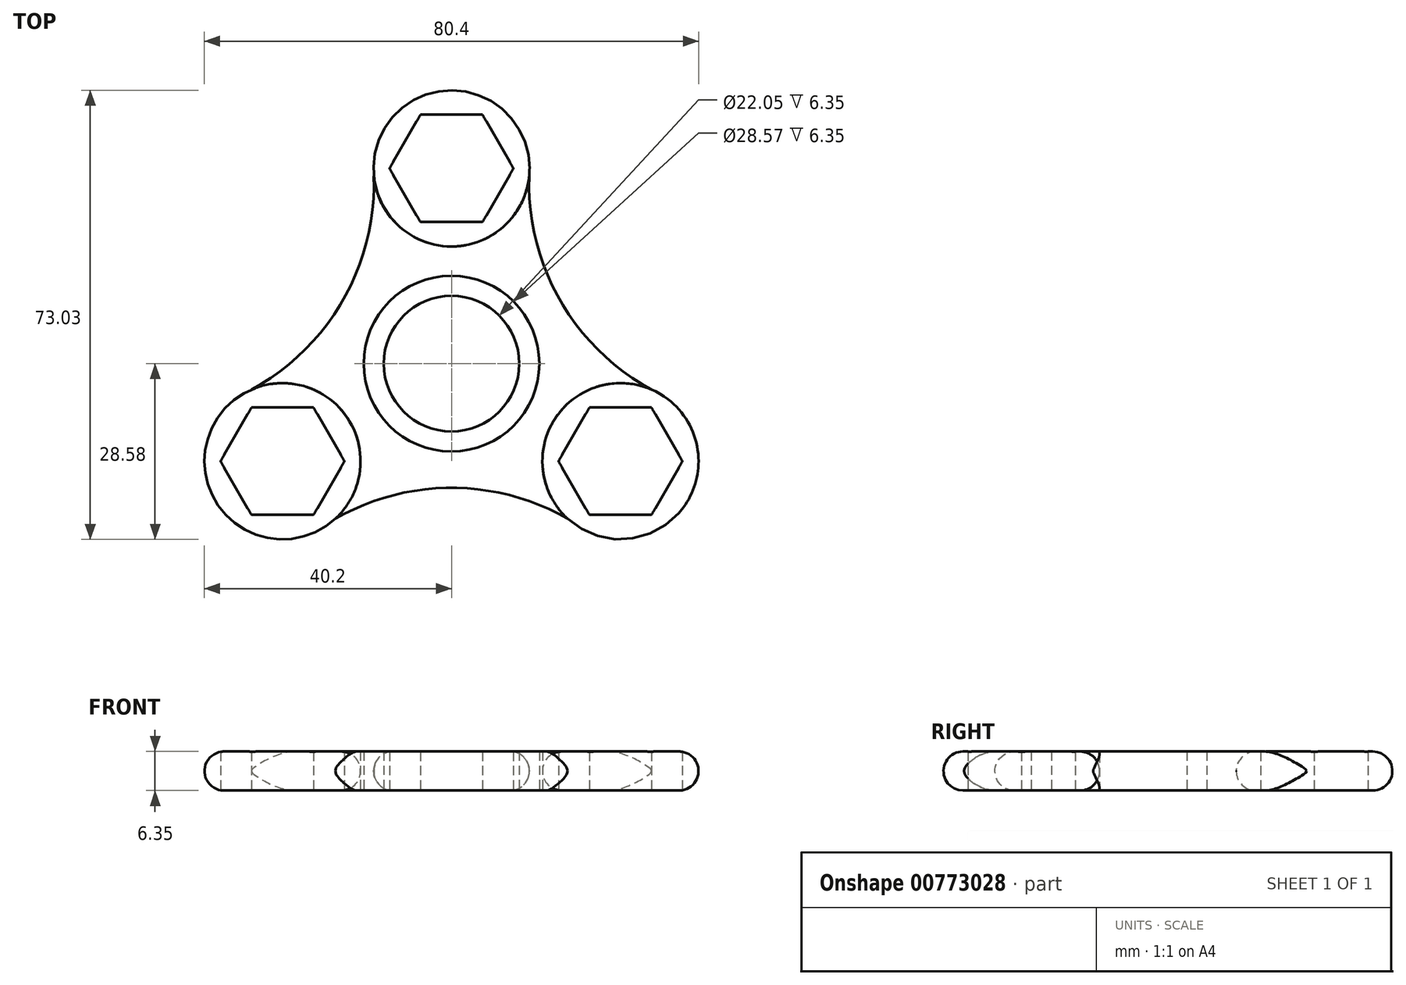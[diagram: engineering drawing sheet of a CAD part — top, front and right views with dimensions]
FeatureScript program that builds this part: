
annotation { "Feature Type Name" : "Feature", "Feature Type Description" : "" }
export const myFeature = defineFeature(function(context is Context, id is Id, definition is map)
    precondition{}
    {
        {
            var Q0;
            Q0=qCreatedBy(makeId("Top.planeOp"),FACE);
            var sketch = newSketch(context, id + "F0", { "sketchPlane" : qUnion([Q0])});
            skCircle(sketch, "E0", {"center": v(0, 0) * mm, "radius": 14.29 * mm});
            skCircle(sketch, "E1", {"center": v(0, 0) * mm, "radius": 11.02 * mm});
            skCircle(sketch, "E2.cCircle", {"center": v(0, 31.75) * mm, "radius": 8.73 * mm, "construction": true});
            skLineSegment(sketch, "E2.0", {"start": v(5.04, 23.02) * mm, "end": v(-5.04, 23.02) * mm});
            skLineSegment(sketch, "E2.1", {"start": v(-5.04, 23.02) * mm, "end": v(-10.08, 31.75) * mm});
            skLineSegment(sketch, "E2.2", {"start": v(-10.08, 31.75) * mm, "end": v(-5.04, 40.48) * mm});
            skLineSegment(sketch, "E2.3", {"start": v(-5.04, 40.48) * mm, "end": v(5.04, 40.48) * mm});
            skLineSegment(sketch, "E2.4", {"start": v(5.04, 40.48) * mm, "end": v(10.08, 31.75) * mm});
            skLineSegment(sketch, "E2.5", {"start": v(10.08, 31.75) * mm, "end": v(5.04, 23.02) * mm});
            skPoint(sketch, "E2.0.midPoint", {"position": v(0, 23.02) * mm});
            skCircle(sketch, "E3", {"center": v(0, 31.75) * mm, "radius": 12.7 * mm});
            skSolve(sketch);
        }
        {
            var Q0;
            Q0=qCreatedBy(makeId("Top.planeOp"),FACE);
            var sketch = newSketch(context, id + "F1", { "sketchPlane" : qUnion([Q0])});
            skLineSegment(sketch, "E4.0", {"start": v(-5.04, 23.02) * mm, "end": v(-10.08, 31.75) * mm});
            skCircle(sketch, "E4.1", {"center": v(0, 31.75) * mm, "radius": 8.73 * mm});
            skCircle(sketch, "E4.2", {"center": v(0, 31.75) * mm, "radius": 12.7 * mm});
            skLineSegment(sketch, "E4.3", {"start": v(10.08, 31.75) * mm, "end": v(5.04, 23.02) * mm});
            skLineSegment(sketch, "E4.4", {"start": v(5.04, 40.48) * mm, "end": v(10.08, 31.75) * mm});
            skLineSegment(sketch, "E4.5", {"start": v(-5.04, 40.48) * mm, "end": v(5.04, 40.48) * mm});
            skLineSegment(sketch, "E4.6", {"start": v(-10.08, 31.75) * mm, "end": v(-5.04, 40.48) * mm});
            skLineSegment(sketch, "E4.7", {"start": v(5.04, 23.02) * mm, "end": v(-5.04, 23.02) * mm});
            skLineSegment(sketch, "E5.1.0", {"start": v(-32.54, -7.14) * mm, "end": v(-22.46, -7.14) * mm});
            skLineSegment(sketch, "E5.1.1", {"start": v(-32.54, -24.6) * mm, "end": v(-37.58, -15.87) * mm});
            skCircle(sketch, "E5.1.2", {"center": v(-27.5, -15.87) * mm, "radius": 12.7 * mm});
            skCircle(sketch, "E5.1.3", {"center": v(-27.5, -15.87) * mm, "radius": 8.73 * mm});
            skLineSegment(sketch, "E5.1.4", {"start": v(-37.58, -15.87) * mm, "end": v(-32.54, -7.14) * mm});
            skLineSegment(sketch, "E5.1.5", {"start": v(-22.46, -24.6) * mm, "end": v(-32.54, -24.6) * mm});
            skLineSegment(sketch, "E5.1.6", {"start": v(-22.46, -7.14) * mm, "end": v(-17.41, -15.87) * mm});
            skLineSegment(sketch, "E5.1.7", {"start": v(-17.41, -15.87) * mm, "end": v(-22.46, -24.6) * mm});
            skLineSegment(sketch, "E5.2.0", {"start": v(22.46, -24.6) * mm, "end": v(17.41, -15.88) * mm});
            skLineSegment(sketch, "E5.2.1", {"start": v(37.58, -15.88) * mm, "end": v(32.54, -24.6) * mm});
            skCircle(sketch, "E5.2.2", {"center": v(27.5, -15.88) * mm, "radius": 12.7 * mm});
            skCircle(sketch, "E5.2.3", {"center": v(27.5, -15.88) * mm, "radius": 8.73 * mm});
            skLineSegment(sketch, "E5.2.4", {"start": v(32.54, -24.6) * mm, "end": v(22.46, -24.6) * mm});
            skLineSegment(sketch, "E5.2.5", {"start": v(32.54, -7.14) * mm, "end": v(37.58, -15.88) * mm});
            skLineSegment(sketch, "E5.2.6", {"start": v(17.41, -15.88) * mm, "end": v(22.46, -7.14) * mm});
            skLineSegment(sketch, "E5.2.7", {"start": v(22.46, -7.14) * mm, "end": v(32.54, -7.14) * mm});
            skPoint(sketch, "E5.center", {"position": v(0, 0) * mm});
            skCircle(sketch, "E6.0", {"center": v(0, 0) * mm, "radius": 11.02 * mm});
            skCircle(sketch, "E6.1", {"center": v(0, 0) * mm, "radius": 14.29 * mm});
            skSolve(sketch);
        }
        {
            var Q0;
            Q0=qCreatedBy(makeId("Top.planeOp"),FACE);
            var sketch = newSketch(context, id + "F2", { "sketchPlane" : qUnion([Q0])});
            skCircle(sketch, "E7.0", {"center": v(0, 31.75) * mm, "radius": 12.7 * mm});
            skCircle(sketch, "E7.1", {"center": v(0, 31.75) * mm, "radius": 8.73 * mm});
            skLineSegment(sketch, "E7.2", {"start": v(10.08, 31.75) * mm, "end": v(5.04, 23.02) * mm});
            skCircle(sketch, "E7.3", {"center": v(-27.5, -15.87) * mm, "radius": 12.7 * mm});
            skCircle(sketch, "E7.4", {"center": v(-27.5, -15.87) * mm, "radius": 8.73 * mm});
            skCircle(sketch, "E7.5", {"center": v(0, 0) * mm, "radius": 11.02 * mm});
            skCircle(sketch, "E7.6", {"center": v(27.5, -15.88) * mm, "radius": 12.7 * mm});
            skCircle(sketch, "E7.7", {"center": v(0, 0) * mm, "radius": 14.29 * mm});
            skCircle(sketch, "E7.8", {"center": v(27.5, -15.88) * mm, "radius": 8.73 * mm});
            skCircle(sketch, "E7.9", {"center": v(0, 0) * mm, "radius": 11.02 * mm});
            skLineSegment(sketch, "E7.10", {"start": v(10.08, 31.75) * mm, "end": v(5.04, 23.02) * mm});
            skLineSegment(sketch, "E7.11", {"start": v(-22.46, -7.14) * mm, "end": v(-17.41, -15.87) * mm});
            skLineSegment(sketch, "E7.12", {"start": v(32.54, -7.14) * mm, "end": v(37.58, -15.88) * mm});
            skLineSegment(sketch, "E7.13", {"start": v(-37.58, -15.87) * mm, "end": v(-32.54, -7.14) * mm});
            skCircle(sketch, "E7.14", {"center": v(0, 0) * mm, "radius": 14.29 * mm});
            skLineSegment(sketch, "E7.15", {"start": v(17.41, -15.88) * mm, "end": v(22.46, -7.14) * mm});
            skCircle(sketch, "E7.16", {"center": v(0, 31.75) * mm, "radius": 12.7 * mm});
            skCircle(sketch, "E7.17", {"center": v(0, 31.75) * mm, "radius": 8.73 * mm});
            skCircle(sketch, "E7.18", {"center": v(0, 31.75) * mm, "radius": 8.73 * mm});
            skLineSegment(sketch, "E7.19", {"start": v(5.04, 23.02) * mm, "end": v(-5.04, 23.02) * mm});
            skCircle(sketch, "E7.20", {"center": v(0, 0) * mm, "radius": 11.02 * mm});
            skCircle(sketch, "E7.21", {"center": v(0, 31.75) * mm, "radius": 12.7 * mm});
            skLineSegment(sketch, "E7.22", {"start": v(10.08, 31.75) * mm, "end": v(5.04, 23.02) * mm});
            skLineSegment(sketch, "E7.23", {"start": v(5.04, 40.48) * mm, "end": v(10.08, 31.75) * mm});
            skLineSegment(sketch, "E7.24", {"start": v(-10.08, 31.75) * mm, "end": v(-5.04, 40.48) * mm});
            skCircle(sketch, "E7.25", {"center": v(0, 0) * mm, "radius": 14.29 * mm});
            skLineSegment(sketch, "E7.26", {"start": v(-5.04, 23.02) * mm, "end": v(-10.08, 31.75) * mm});
            skLineSegment(sketch, "E7.27", {"start": v(-5.04, 40.48) * mm, "end": v(5.04, 40.48) * mm});
            skLineSegment(sketch, "E7.28", {"start": v(-5.04, 23.02) * mm, "end": v(-10.08, 31.75) * mm});
            skLineSegment(sketch, "E7.29", {"start": v(-5.04, 40.48) * mm, "end": v(5.04, 40.48) * mm});
            skArc(sketch, "E8", {"start": v(-32.54, -4.22) * mm, "mid": v(-17.35, 10.86) * mm, "end": v(-12.7, 31.75) * mm});
            skArc(sketch, "E9", {"start": v(22.47, -27.54) * mm, "mid": v(0, -20.2) * mm, "end": v(-22.46, -27.53) * mm});
            skArc(sketch, "E10", {"start": v(12.7, 31.75) * mm, "mid": v(17.35, 10.86) * mm, "end": v(32.54, -4.22) * mm});
            skLineSegment(sketch, "E11.1", {"start": v(-32.54, -24.6) * mm, "end": v(-37.58, -15.87) * mm});
            skSolve(sketch);
        }
        {
            var Q0;
            Q0=makeQuery(id+"F1.imprint","IMPRINT",FACE,{"disambiguationData":[TD([[makeQuery(id+"F1.imprint","IMPRINT",EDGE,{"derivedFrom":sQuery(id+"F1.wireOp",EDGE,"E5.1.2")}),1.0]])]});
            var Q1;
            Q1=makeQuery(id+"F0.imprint","IMPRINT",FACE,{"disambiguationData":[TD([[makeQuery(id+"F0.imprint","IMPRINT",EDGE,{"derivedFrom":sQuery(id+"F0.wireOp",EDGE,"E2.0")}),1.0]])]});
            var Q2;
            Q2=makeQuery(id+"F1.imprint","IMPRINT",FACE,{"disambiguationData":[TD([[makeQuery(id+"F1.imprint","IMPRINT",EDGE,{"derivedFrom":sQuery(id+"F1.wireOp",EDGE,"E5.2.2")}),1.0]])]});
            var Q3;
            Q3=makeQuery(id+"F0.imprint","IMPRINT",FACE,{"disambiguationData":[TD([[makeQuery(id+"F0.imprint","IMPRINT",EDGE,{"derivedFrom":sQuery(id+"F0.wireOp",EDGE,"E0")}),1.0]])]});
            var Q4;
            Q4=makeQuery(id+"F2.imprint","IMPRINT",FACE,{"disambiguationData":[TD([[makeQuery(id+"F2.imprint","IMPRINT",EDGE,{"derivedFrom":sQuery(id+"F2.wireOp",EDGE,"E7.7")}),-1.0]])]});
            extrude(context, id + "F3", {"entities" : qUnion([Q0, Q1, Q2, Q3, Q4]), "depth" : 6.35 * mm, "offsetDistance" : 25.4 * mm});
        }
        {
            var Q0;
            Q0=makeQuery(id+"F3.opExtrude","CAP_EDGE",EDGE,{"disambiguationData":[OSD([sQuery(id+"F2.wireOp",EDGE,"E8")])],"isStart":false});
            var Q1;
            Q1=makeQuery(id+"F3.opExtrude","CAP_EDGE",EDGE,{"disambiguationData":[OSD([sQuery(id+"F1.wireOp",EDGE,"E5.1.2")])],"isStart":false});
            var Q2;
            Q2=makeQuery(id+"F3.opExtrude","CAP_EDGE",EDGE,{"disambiguationData":[OSD([sQuery(id+"F2.wireOp",EDGE,"E9")])],"isStart":false});
            var Q3;
            Q3=makeQuery(id+"F3.opExtrude","CAP_EDGE",EDGE,{"disambiguationData":[OSD([sQuery(id+"F1.wireOp",EDGE,"E5.2.2")])],"isStart":false});
            var Q4;
            Q4=makeQuery(id+"F3.opExtrude","CAP_EDGE",EDGE,{"disambiguationData":[OSD([sQuery(id+"F2.wireOp",EDGE,"E10")])],"isStart":false});
            var Q5;
            Q5=makeQuery(id+"F3.opExtrude","CAP_EDGE",EDGE,{"disambiguationData":[OSD([sQuery(id+"F0.wireOp",EDGE,"E3")])],"isStart":false});
            fillet(context, id + "F4", {"entities" : qUnion([Q0, Q1, Q2, Q3, Q4, Q5]), "radius" : 3.17 * mm, "tangentPropagation" : true, "allowEdgeOverflow" : false});
        }
        {
            var Q0;
            Q0=makeQuery(id+"F3.opExtrude","CAP_EDGE",EDGE,{"disambiguationData":[OSD([sQuery(id+"F2.wireOp",EDGE,"E10")])],"isStart":true});
            var Q1;
            Q1=makeQuery(id+"F3.opExtrude","CAP_EDGE",EDGE,{"disambiguationData":[OSD([sQuery(id+"F1.wireOp",EDGE,"E5.2.2")])],"isStart":true});
            var Q2;
            Q2=makeQuery(id+"F3.opExtrude","CAP_EDGE",EDGE,{"disambiguationData":[OSD([sQuery(id+"F1.wireOp",EDGE,"E5.1.2")])],"isStart":true});
            var Q3;
            Q3=makeQuery(id+"F3.opExtrude","CAP_EDGE",EDGE,{"disambiguationData":[OSD([sQuery(id+"F2.wireOp",EDGE,"E9")])],"isStart":true});
            var Q4;
            Q4=makeQuery(id+"F3.opExtrude","CAP_EDGE",EDGE,{"disambiguationData":[OSD([sQuery(id+"F2.wireOp",EDGE,"E8")])],"isStart":true});
            var Q5;
            Q5=makeQuery(id+"F3.opExtrude","CAP_EDGE",EDGE,{"disambiguationData":[OSD([sQuery(id+"F0.wireOp",EDGE,"E3")])],"isStart":true});
            fillet(context, id + "F5", {"entities" : qUnion([Q0, Q1, Q2, Q3, Q4, Q5]), "radius" : 3.17 * mm, "tangentPropagation" : true, "allowEdgeOverflow" : false});
        }
    });
